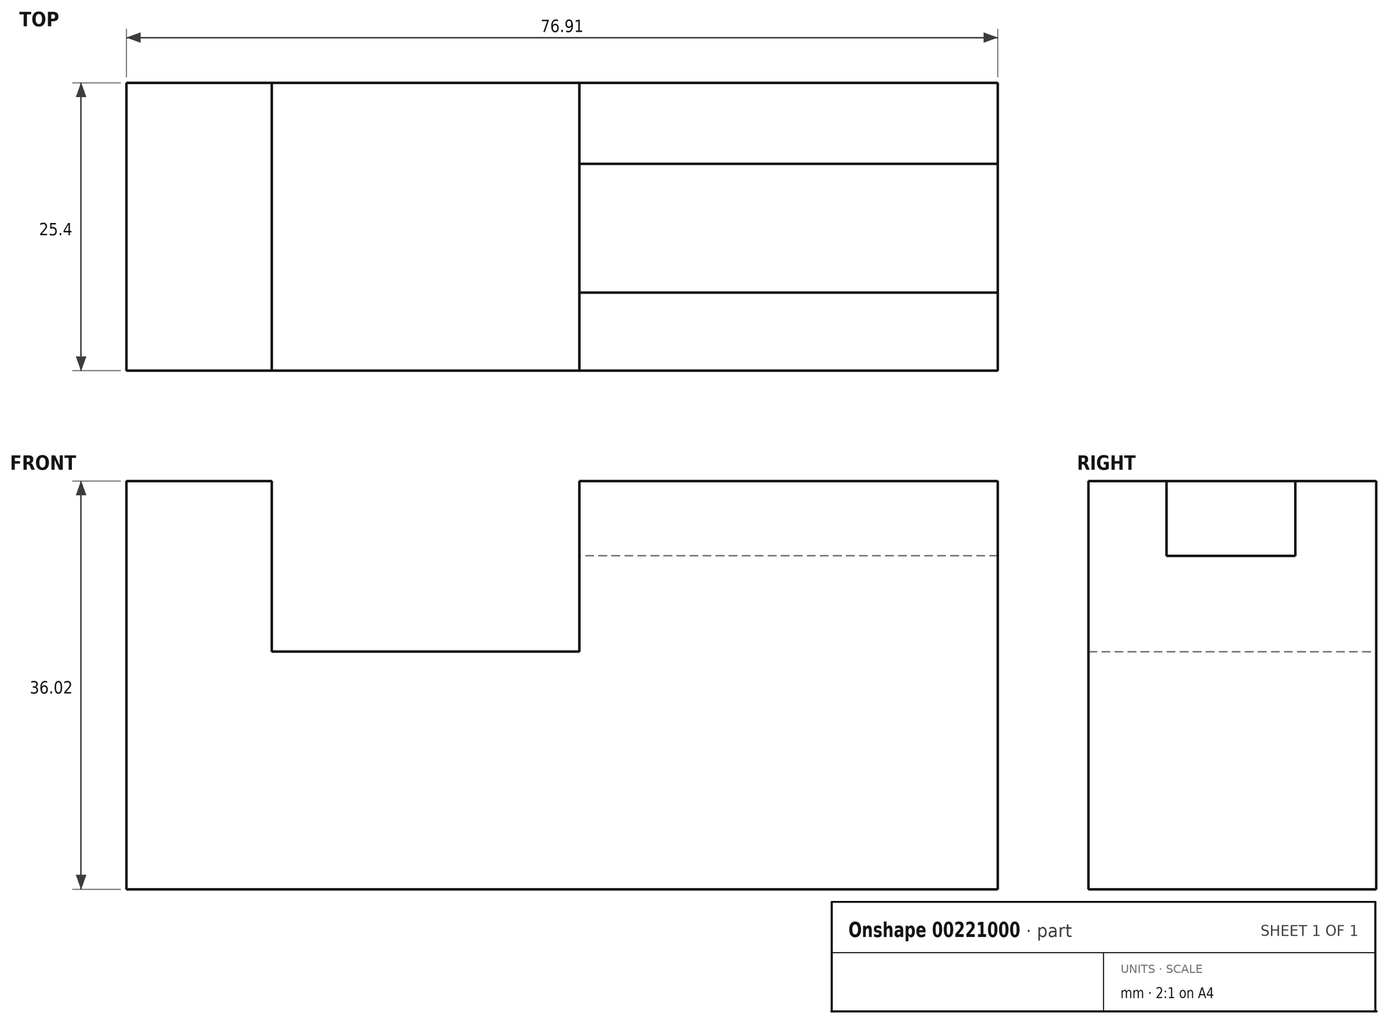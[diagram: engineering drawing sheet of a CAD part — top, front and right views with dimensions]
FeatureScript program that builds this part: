
annotation { "Feature Type Name" : "Feature", "Feature Type Description" : "" }
export const myFeature = defineFeature(function(context is Context, id is Id, definition is map)
    precondition{}
    {
        {
            var Q0;
            Q0=qCreatedBy(makeId("Front.planeOp"),FACE);
            var sketch = newSketch(context, id + "F0", { "sketchPlane" : qUnion([Q0])});
            skLineSegment(sketch, "E0", {"start": v(0, 36.02) * mm, "end": v(51.5, 36.02) * mm});
            skLineSegment(sketch, "E1", {"start": v(51.5, 36.02) * mm, "end": v(51.5, 0) * mm});
            skLineSegment(sketch, "E2", {"start": v(0, 0) * mm, "end": v(51.5, 0) * mm});
            skLineSegment(sketch, "E3", {"start": v(0, 36.02) * mm, "end": v(0, 0) * mm});
            skLineSegment(sketch, "E4", {"start": v(12.83, 36.02) * mm, "end": v(12.83, 20.99) * mm});
            skLineSegment(sketch, "E5", {"start": v(12.83, 20.99) * mm, "end": v(39.96, 20.99) * mm});
            skLineSegment(sketch, "E6", {"start": v(39.96, 20.99) * mm, "end": v(39.96, 36.02) * mm});
            skSolve(sketch);
        }
        {
            var Q0;
            {var subQ0=sQuery(id+"F0.wireOp",EDGE,"E1");Q0=makeQuery(id+"F0.imprint","IMPRINT",FACE,{"disambiguationData":[TD([[makeQuery(id+"F0.imprint","IMPRINT",EDGE,{"derivedFrom":subQ0}),-1.0]])]});}
            extrude(context, id + "F1", {"entities" : qUnion([Q0]), "depth" : 25.4 * mm});
        }
        {
            var Q0;
            Q0=makeQuery(id+"F1.opExtrude","SWEPT_FACE",FACE,{"disambiguationData":[OSD([sQuery(id+"F0.wireOp",EDGE,"E1")])]});
            var sketch = newSketch(context, id + "F2", { "sketchPlane" : qUnion([Q0])});
            skLineSegment(sketch, "E7", {"start": v(-18.51, 36.02) * mm, "end": v(-18.51, 29.42) * mm});
            skLineSegment(sketch, "E8", {"start": v(-18.51, 29.42) * mm, "end": v(-7.15, 29.42) * mm});
            skLineSegment(sketch, "E9", {"start": v(-7.15, 29.42) * mm, "end": v(-7.15, 36.02) * mm});
            skSolve(sketch);
        }
        {
            var Q0;
            Q0 = qSketchRegion(id + "F2", true);
            var Q1;
            {var subQ2=sQuery(id+"F2.wireOp",EDGE,"E7");Q1=makeQuery(id+"F2.imprint","IMPRINT",FACE,{"disambiguationData":[TD([[makeQuery(id+"F2.imprint","IMPRINT",EDGE,{"derivedFrom":subQ2}),-1.0]])]});}
            extrude(context, id + "F3", {"entities" : qUnion([Q0, Q1]), "operationType" : NewBodyOperationType.ADD, "depth" : 25.4 * mm});
        }
        {
            var Q0;
            Q0=makeQuery(id+"F1.opExtrude","SWEPT_FACE",FACE,{"disambiguationData":[OSD([sQuery(id+"F0.wireOp",EDGE,"E1")])]});
            extrude(context, id + "F4", {"entities" : qUnion([Q0]), "operationType" : NewBodyOperationType.REMOVE, "oppositeDirection" : true, "depth" : 25.4 * mm});
        }
    });
